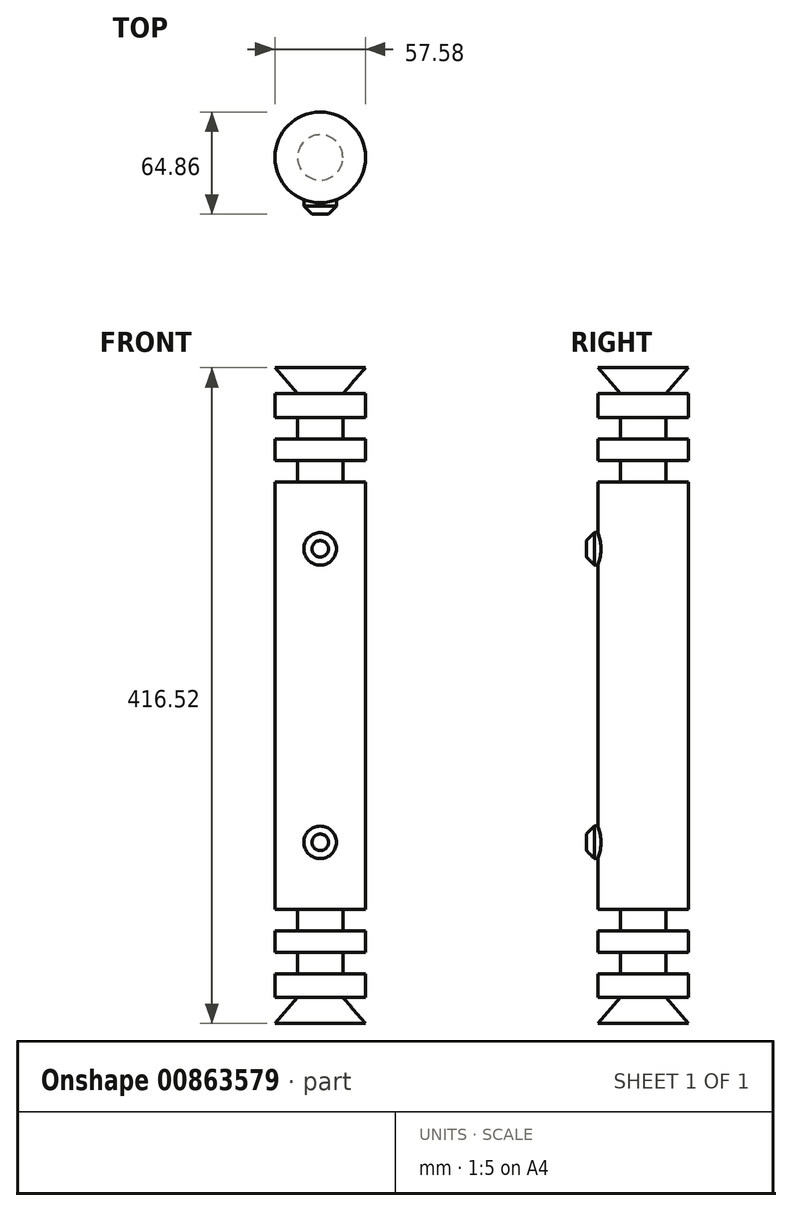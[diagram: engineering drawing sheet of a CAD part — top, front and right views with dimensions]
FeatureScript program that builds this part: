
annotation { "Feature Type Name" : "Feature", "Feature Type Description" : "" }
export const myFeature = defineFeature(function(context is Context, id is Id, definition is map)
    precondition{}
    {
        {
            var Q0;
            Q0=qCreatedBy(makeId("Front.planeOp"),FACE);
            var sketch = newSketch(context, id + "F0", { "sketchPlane" : qUnion([Q0])});
            skLineSegment(sketch, "E0", {"start": v(0, 0) * mm, "end": v(0, -208.26) * mm});
            skLineSegment(sketch, "E1", {"start": v(0, -208.26) * mm, "end": v(28.8, -208.26) * mm});
            skLineSegment(sketch, "E2", {"start": v(28.8, -208.26) * mm, "end": v(14.4, -191.83) * mm});
            skPoint(sketch, "E2.endSnap0", {"position": v(14.4, -208.26) * mm});
            skLineSegment(sketch, "E3", {"start": v(14.4, -191.83) * mm, "end": v(28.8, -191.83) * mm});
            skLineSegment(sketch, "E4", {"start": v(28.8, -191.83) * mm, "end": v(28.8, -176.77) * mm});
            skLineSegment(sketch, "E5", {"start": v(14.4, -176.77) * mm, "end": v(28.8, -176.77) * mm});
            skLineSegment(sketch, "E6", {"start": v(14.4, -176.77) * mm, "end": v(14.4, -163.08) * mm});
            skLineSegment(sketch, "E7", {"start": v(28.8, -163.08) * mm, "end": v(14.4, -163.08) * mm});
            skLineSegment(sketch, "E8", {"start": v(28.8, -163.08) * mm, "end": v(28.8, -149.4) * mm});
            skLineSegment(sketch, "E9", {"start": v(14.4, -149.4) * mm, "end": v(28.8, -149.4) * mm});
            skLineSegment(sketch, "E10", {"start": v(14.4, -149.4) * mm, "end": v(14.4, -135.7) * mm});
            skLineSegment(sketch, "E11", {"start": v(14.4, -135.7) * mm, "end": v(28.8, -135.7) * mm});
            skLineSegment(sketch, "E12", {"start": v(28.8, -135.7) * mm, "end": v(28.8, 0) * mm});
            skLineSegment(sketch, "E13", {"start": v(28.8, 0) * mm, "end": v(0, 0) * mm});
            skLineSegment(sketch, "E14.MirrorCS", {"start": v(28.8, 135.7) * mm, "end": v(28.8, 0) * mm});
            skLineSegment(sketch, "E15.MirrorCS", {"start": v(28.8, 208.26) * mm, "end": v(14.4, 191.83) * mm});
            skLineSegment(sketch, "E16.MirrorCS", {"start": v(0, 208.26) * mm, "end": v(28.8, 208.26) * mm});
            skLineSegment(sketch, "E17.MirrorCS", {"start": v(14.4, 176.77) * mm, "end": v(14.4, 163.08) * mm});
            skLineSegment(sketch, "E18.MirrorCS", {"start": v(14.4, 191.83) * mm, "end": v(28.8, 191.83) * mm});
            skLineSegment(sketch, "E19.MirrorCS", {"start": v(28.8, 163.08) * mm, "end": v(28.8, 149.4) * mm});
            skLineSegment(sketch, "E20.MirrorCS", {"start": v(28.8, 163.08) * mm, "end": v(14.4, 163.08) * mm});
            skLineSegment(sketch, "E21.MirrorCS", {"start": v(14.4, 149.4) * mm, "end": v(14.4, 135.7) * mm});
            skLineSegment(sketch, "E22.MirrorCS", {"start": v(14.4, 149.4) * mm, "end": v(28.8, 149.4) * mm});
            skLineSegment(sketch, "E23.MirrorCS", {"start": v(28.8, 191.83) * mm, "end": v(28.8, 176.77) * mm});
            skLineSegment(sketch, "E24.MirrorCS", {"start": v(14.4, 176.77) * mm, "end": v(28.8, 176.77) * mm});
            skLineSegment(sketch, "E25.MirrorCS", {"start": v(14.4, 135.7) * mm, "end": v(28.8, 135.7) * mm});
            skLineSegment(sketch, "E26.MirrorCS", {"start": v(0, 0) * mm, "end": v(0, 208.26) * mm});
            skPoint(sketch, "E27.MirrorP", {"position": v(14.4, 208.26) * mm});
            skSolve(sketch);
        }
        {
            var Q0;
            Q0=makeQuery(id+"F0.imprint","IMPRINT",FACE,{"disambiguationData":[TD([[makeQuery(id+"F0.imprint","IMPRINT",EDGE,{"derivedFrom":sQuery(id+"F0.wireOp",EDGE,"E13")}),-1.0]])]});
            var Q1;
            Q1=makeQuery(id+"F0.imprint","IMPRINT",FACE,{"disambiguationData":[TD([[makeQuery(id+"F0.imprint","IMPRINT",EDGE,{"derivedFrom":sQuery(id+"F0.wireOp",EDGE,"E0")}),1.0]])]});
            var Q2;
            Q2=sQuery(id+"F0.wireOp",EDGE,"E0");
            revolve(context, id + "F1", {"surfaceOperationType" : NewSurfaceOperationType.NEW, "entities" : qUnion([Q0, Q1]), "axis" : qUnion([Q2]), "revolveType" : RevolveType.FULL});
        }
        {
            var Q0;
            Q0=qCreatedBy(makeId("Front.planeOp"),FACE);
            var sketch = newSketch(context, id + "F2", { "sketchPlane" : qUnion([Q0])});
            skCircle(sketch, "E28", {"center": v(0, 93.21) * mm, "radius": 10.32 * mm});
            skCircle(sketch, "E29.MirrorC", {"center": v(0, -93.21) * mm, "radius": 10.32 * mm});
            skSolve(sketch);
        }
        {
            var Q0;
            Q0 = qSketchRegion(id + "F2", true);
            extrude(context, id + "F3", {"entities" : qUnion([Q0]), "operationType" : NewBodyOperationType.ADD, "depth" : 36.07 * mm, "offsetDistance" : 25.4 * mm});
        }
        {
            var Q0;
            Q0=makeQuery(id+"F3.opExtrude","CAP_EDGE",EDGE,{"disambiguationData":[OSD([sQuery(id+"F2.wireOp",EDGE,"E28")])],"isStart":false});
            var Q1;
            Q1=makeQuery(id+"F3.opExtrude","CAP_EDGE",EDGE,{"disambiguationData":[OSD([sQuery(id+"F2.wireOp",EDGE,"E29.MirrorC")])],"isStart":false});
            chamfer(context, id + "F4", {"entities" : qUnion([Q0, Q1]), "width" : 5.08 * mm, "tangentPropagation" : true});
        }
    });
